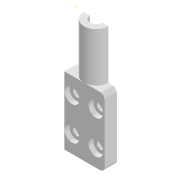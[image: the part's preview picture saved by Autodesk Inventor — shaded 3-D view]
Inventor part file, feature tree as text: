
AUTODESK INVENTOR PART (.ipt)
format: ipt  version: 2020.3 (Build 243373000, 373)  size: 173,056 bytes
history: native  units: mm
features: reference x11, sketch x8, extrude x7, other x3, fillet x1, projected_geometry x1
ambient origin geometry x8: Origin, YZ Plane, XZ Plane, XY Plane, X Axis, Y Axis, Z Axis, Center Point
bodies: Volumenkörper1 (feature_tree)
feature tree (31):
  extrude  "Extrusion1"  Depth=5.0mm TaperAngle=0.0deg
  extrude  "Extrusion2"  Depth=2.5mm
  extrude  "Extrusion3"  TaperAngle=0.0deg  [1 undecoded]
  extrude  "Extrusion4"  Depth=0.7mm
  fillet  "Rundung1"  [1 undecoded]
  extrude  "Extrusion5"  Depth=2.5mm
  extrude  "Extrusion7"  Depth=20.0mm TaperAngle=0.0deg
  sketch  "Skizze8"  dims[d18=6.0mm d19=2.0mm d20=0.0mm]
  extrude  "Extrusion8"  Depth=2.0mm TaperAngle=0.0deg
  sketch  "Skizze1"  dims[d0=0.5mm d1=5.0mm d2=0.0mm]
  reference  "Referenz1"
  reference  "Referenz2"
  sketch  "Skizze2"  dims[d3=10.0mm d4=0.0mm d5=2.5mm]
  reference  "Referenz3"
  reference  "Referenz4"
  reference  "Referenz5"
  reference  "Referenz6"
  sketch  "Skizze3"  dims[d6=1.25mm d7=0.0mm]
  reference  "Referenz7"
  reference  "Referenz8"
  reference  "Referenz9"
  sketch  "Skizze4"  dims[d8=1.4mm d9=0.7mm d10=0.0mm]
  reference  "Referenz10"
  reference  "Referenz11"
  sketch  "Skizze5"  dims[d11=2.0mm d12=2.5mm]
  sketch  "Skizze7"  dims[d13=0.0mm d14=20.0mm d15=0.0mm]
  sketch  "Skizze9"  dims[d21=2.0mm d22=0.0mm]
  projected_geometry  "Projizierte Kontur2"
  other  "<userpath>\SynologyDrive\WiMi\RobotikMaschinen\HeleneRoboterarm\KraftMessNadel\Gesamt.iam"
  other  "Gesamt.iam"
  other  "NadelhalterSchraub:1"
note: 2 required parameter values undecoded (feature->parameter linkage not recoverable at this tier; creation-order binding heuristic only, values carry confidence <= 0.55)
